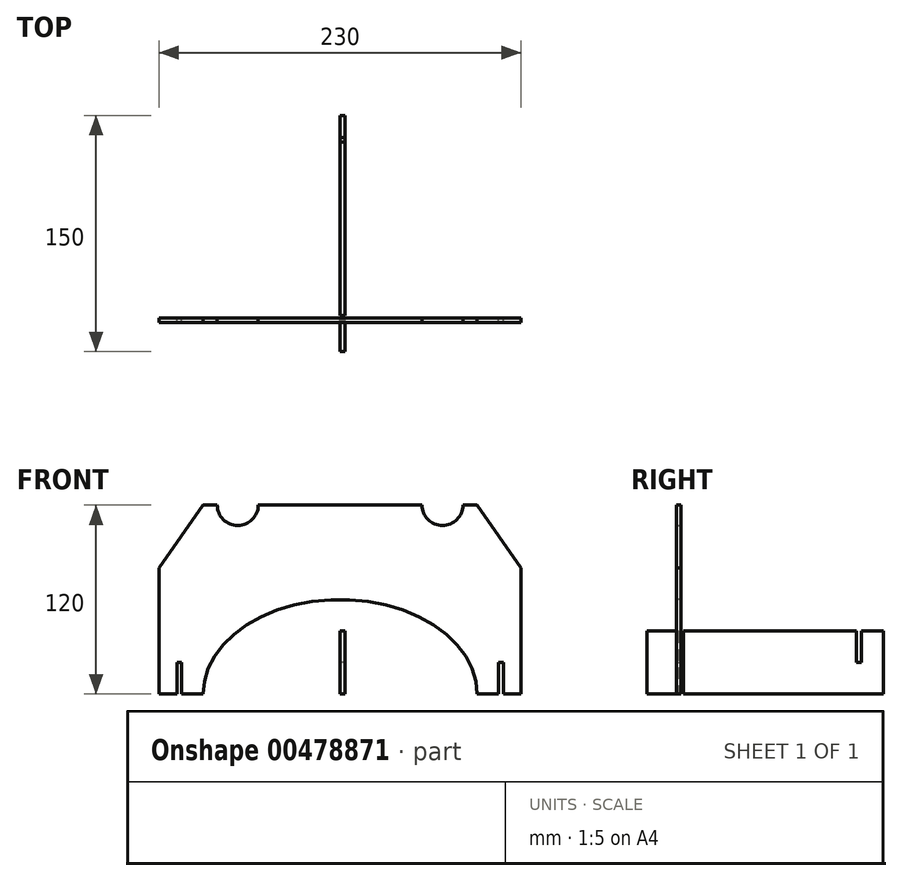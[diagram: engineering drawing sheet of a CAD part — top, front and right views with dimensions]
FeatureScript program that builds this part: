
annotation { "Feature Type Name" : "Feature", "Feature Type Description" : "" }
export const myFeature = defineFeature(function(context is Context, id is Id, definition is map)
    precondition{}
    {
        {
            var Q0;
            Q0=qCreatedBy(makeId("Front.planeOp"),FACE);
            var sketch = newSketch(context, id + "F0", { "sketchPlane" : qUnion([Q0])});
            skLineSegment(sketch, "E0.bottom", {"start": v(-65, 60) * mm, "end": v(65, 60) * mm, "construction": true});
            skLineSegment(sketch, "E0.top", {"start": v(-65, -60) * mm, "end": v(65, -60) * mm, "construction": true});
            skLineSegment(sketch, "E0.left", {"start": v(-65, 60) * mm, "end": v(-65, -60) * mm, "construction": true});
            skLineSegment(sketch, "E0.right", {"start": v(65, 60) * mm, "end": v(65, -60) * mm, "construction": true});
            skPoint(sketch, "E0.middle", {"position": v(0, 0) * mm});
            skLineSegment(sketch, "E1.bottom", {"start": v(65, -60) * mm, "end": v(115, -60) * mm, "construction": true});
            skLineSegment(sketch, "E1.top", {"start": v(65, 60) * mm, "end": v(115, 60) * mm, "construction": true});
            skLineSegment(sketch, "E1.left", {"start": v(65, -60) * mm, "end": v(65, 60) * mm, "construction": true});
            skLineSegment(sketch, "E1.right", {"start": v(115, -60) * mm, "end": v(115, 60) * mm, "construction": true});
            skLineSegment(sketch, "E2.bottom", {"start": v(-65, -60) * mm, "end": v(-115, -60) * mm, "construction": true});
            skLineSegment(sketch, "E2.top", {"start": v(-65, 60) * mm, "end": v(-115, 60) * mm, "construction": true});
            skLineSegment(sketch, "E2.left", {"start": v(-65, -60) * mm, "end": v(-65, 60) * mm, "construction": true});
            skLineSegment(sketch, "E2.right", {"start": v(-115, -60) * mm, "end": v(-115, 60) * mm, "construction": true});
            skCircle(sketch, "E3", {"center": v(65, 60) * mm, "radius": 13 * mm});
            skCircle(sketch, "E4", {"center": v(-65, 60) * mm, "radius": 13 * mm});
            skLineSegment(sketch, "E5", {"start": v(87, 60) * mm, "end": v(115, 20) * mm, "construction": true});
            skLineSegment(sketch, "E6", {"start": v(115, 20) * mm, "end": v(-115, 20) * mm, "construction": true});
            skLineSegment(sketch, "E7", {"start": v(-115, 20) * mm, "end": v(-87, 60) * mm, "construction": true});
            skLineSegment(sketch, "E8", {"start": v(-115, 20) * mm, "end": v(-87, 60) * mm});
            skLineSegment(sketch, "E9", {"start": v(-115, 20) * mm, "end": v(-115, -60) * mm});
            skLineSegment(sketch, "E10", {"start": v(115, -60) * mm, "end": v(-115, -60) * mm});
            skLineSegment(sketch, "E11", {"start": v(115, -60) * mm, "end": v(115, 20) * mm});
            skLineSegment(sketch, "E12", {"start": v(115, 20) * mm, "end": v(87, 60) * mm});
            skPoint(sketch, "E13", {"position": v(52, 60) * mm});
            skPoint(sketch, "E14", {"position": v(78, 60) * mm});
            skPoint(sketch, "E15", {"position": v(-52, 60) * mm});
            skPoint(sketch, "E16", {"position": v(-78, 60) * mm});
            skLineSegment(sketch, "E17", {"start": v(-87, 60) * mm, "end": v(-78, 60) * mm});
            skLineSegment(sketch, "E18", {"start": v(-52, 60) * mm, "end": v(52, 60) * mm});
            skLineSegment(sketch, "E19", {"start": v(78, 60) * mm, "end": v(87, 60) * mm});
            skLineSegment(sketch, "E20", {"start": v(87, 60) * mm, "end": v(87, -67.3) * mm, "construction": true});
            skPoint(sketch, "E21", {"position": v(87, -60) * mm});
            skLineSegment(sketch, "E22.bottom", {"start": v(-103.62, -60) * mm, "end": v(-100.62, -60) * mm});
            skLineSegment(sketch, "E22.top", {"start": v(-103.62, -40) * mm, "end": v(-100.62, -40) * mm});
            skLineSegment(sketch, "E22.left", {"start": v(-103.62, -60) * mm, "end": v(-103.62, -40) * mm});
            skLineSegment(sketch, "E22.right", {"start": v(-100.62, -60) * mm, "end": v(-100.62, -40) * mm});
            skLineSegment(sketch, "E23.MirrorCS", {"start": v(100.62, -60) * mm, "end": v(100.62, -40) * mm});
            skLineSegment(sketch, "E24.MirrorCS", {"start": v(103.62, -60) * mm, "end": v(103.62, -40) * mm});
            skLineSegment(sketch, "E25.MirrorCS", {"start": v(103.62, -40) * mm, "end": v(100.62, -40) * mm});
            skEllipse(sketch, "E26", {"center": v(0, -60) * mm, "majorRadius": 87 * mm, "minorRadius": 60 * mm, "majorAxis": v(1, 0)});
            skFitSpline(sketch, "E27.0", {"points": [v(101.9, -64.06) * mm, v(102.05, -60) * mm, v(101.9, -55.94) * mm, v(101.32, -50.58) * mm, v(99.9, -44.01) * mm, v(97.13, -36.44) * mm, v(93.39, -29.24) * mm, v(88.75, -22.49) * mm, v(84.2, -17.25) * mm, v(80.18, -13.3) * mm, v(76.99, -10.48) * mm, v(74.17, -8.23) * mm, v(71.84, -6.49) * mm, v(70.04, -5.22) * mm, v(68.2, -3.99) * mm, v(65.72, -2.4) * mm, v(62.54, -0.5) * mm, v(58.6, 1.61) * mm, v(53.2, 4.23) * mm, v(46.2, 7.11) * mm, v(37.46, 9.96) * mm, v(28.42, 12.2) * mm, v(20.68, 13.53) * mm, v(14.4, 14.3) * mm, v(9.63, 14.7) * mm, v(5.63, 14.9) * mm, v(2.42, 14.99) * mm, v(0, 15) * mm, v(-2.42, 14.99) * mm, v(-5.63, 14.9) * mm, v(-9.63, 14.7) * mm, v(-14.4, 14.3) * mm, v(-20.68, 13.53) * mm, v(-28.42, 12.2) * mm, v(-37.46, 9.96) * mm, v(-46.2, 7.11) * mm, v(-53.2, 4.23) * mm, v(-58.6, 1.61) * mm, v(-62.54, -0.5) * mm, v(-65.72, -2.4) * mm, v(-68.2, -3.99) * mm, v(-70.04, -5.22) * mm, v(-71.84, -6.49) * mm, v(-74.17, -8.23) * mm, v(-76.99, -10.48) * mm, v(-80.18, -13.3) * mm, v(-84.2, -17.25) * mm, v(-88.75, -22.49) * mm, v(-93.39, -29.24) * mm, v(-97.13, -36.44) * mm, v(-99.9, -44.01) * mm, v(-101.32, -50.58) * mm, v(-101.9, -55.94) * mm, v(-102.05, -60) * mm, v(-101.9, -64.06) * mm, v(-101.32, -69.42) * mm, v(-99.9, -75.99) * mm, v(-97.13, -83.56) * mm, v(-93.39, -90.76) * mm, v(-88.75, -97.51) * mm, v(-84.2, -102.75) * mm, v(-80.18, -106.7) * mm, v(-76.99, -109.52) * mm, v(-74.17, -111.77) * mm, v(-71.84, -113.51) * mm, v(-70.04, -114.78) * mm, v(-68.2, -116.01) * mm, v(-65.72, -117.6) * mm, v(-62.54, -119.5) * mm, v(-58.6, -121.61) * mm, v(-53.2, -124.23) * mm, v(-46.2, -127.11) * mm, v(-37.46, -129.96) * mm, v(-28.42, -132.2) * mm, v(-20.68, -133.53) * mm, v(-14.4, -134.3) * mm, v(-9.63, -134.7) * mm, v(-5.63, -134.9) * mm, v(-2.42, -134.99) * mm, v(0, -135) * mm, v(2.42, -134.99) * mm, v(5.63, -134.9) * mm, v(9.63, -134.7) * mm, v(14.4, -134.3) * mm, v(20.68, -133.53) * mm, v(28.42, -132.2) * mm, v(37.46, -129.96) * mm, v(46.2, -127.11) * mm, v(53.2, -124.23) * mm, v(58.6, -121.61) * mm, v(62.54, -119.5) * mm, v(65.72, -117.6) * mm, v(68.2, -116.01) * mm, v(70.04, -114.78) * mm, v(71.84, -113.51) * mm, v(74.17, -111.77) * mm, v(76.99, -109.52) * mm, v(80.18, -106.7) * mm, v(84.2, -102.75) * mm, v(88.75, -97.51) * mm, v(93.39, -90.76) * mm, v(97.13, -83.56) * mm, v(99.9, -75.99) * mm, v(101.32, -69.42) * mm, v(101.9, -64.06) * mm, v(102.05, -60) * mm, v(101.9, -55.94) * mm, v(101.9, -64.06) * mm], "construction": true});
            skPoint(sketch, "E28", {"position": v(102, -60) * mm});
            skPoint(sketch, "E29", {"position": v(-102, -60) * mm});
            skSolve(sketch);
        }
        {
            var Q0;
            Q0=makeQuery(id+"F0.imprint","IMPRINT",FACE,{"disambiguationData":[TD([[makeQuery(id+"F0.imprint","IMPRINT",EDGE,{"derivedFrom":sQuery(id+"F0.wireOp",EDGE,"E8")}),-1.0]])]});
            extrude(context, id + "F1", {"entities" : qUnion([Q0]), "depth" : 3 * mm});
        }
        {
            var Q0;
            Q0=qCreatedBy(makeId("Right.planeOp"),FACE);
            var sketch = newSketch(context, id + "F2", { "sketchPlane" : qUnion([Q0])});
            skLineSegment(sketch, "E30.bottom", {"start": v(-21.5, -60) * mm, "end": v(128.5, -60) * mm});
            skLineSegment(sketch, "E30.top", {"start": v(-21.5, -20) * mm, "end": v(128.5, -20) * mm});
            skLineSegment(sketch, "E30.left", {"start": v(-21.5, -60) * mm, "end": v(-21.5, -20) * mm});
            skLineSegment(sketch, "E30.right", {"start": v(128.5, -60) * mm, "end": v(128.5, -20) * mm});
            skPoint(sketch, "E31.0", {"position": v(0, -40) * mm});
            skLineSegment(sketch, "E32.bottom", {"start": v(-1.5, -20) * mm, "end": v(1.5, -20) * mm});
            skLineSegment(sketch, "E32.top", {"start": v(-1.5, -60) * mm, "end": v(1.5, -60) * mm});
            skLineSegment(sketch, "E32.left", {"start": v(-1.5, -20) * mm, "end": v(-1.5, -60) * mm});
            skLineSegment(sketch, "E32.right", {"start": v(1.5, -20) * mm, "end": v(1.5, -60) * mm});
            skLineSegment(sketch, "E33", {"start": v(0, -40) * mm, "end": v(1.5, -40) * mm});
            skLineSegment(sketch, "E34", {"start": v(0, -40) * mm, "end": v(-1.5, -40) * mm});
            skLineSegment(sketch, "E35", {"start": v(1.5, -20) * mm, "end": v(111.5, -20) * mm, "construction": true});
            skLineSegment(sketch, "E36", {"start": v(56.5, -20) * mm, "end": v(56.5, -66.14) * mm, "construction": true});
            skLineSegment(sketch, "E37.MirrorCS", {"start": v(114.5, -20) * mm, "end": v(114.5, -60) * mm});
            skLineSegment(sketch, "E38.MirrorCS", {"start": v(111.5, -20) * mm, "end": v(111.5, -60) * mm});
            skLineSegment(sketch, "E39.MirrorCS", {"start": v(113, -40) * mm, "end": v(114.5, -40) * mm});
            skLineSegment(sketch, "E40.MirrorCS", {"start": v(113, -40) * mm, "end": v(111.5, -40) * mm});
            skSolve(sketch);
        }
        {
            var Q0;
            {var subQ1=sQuery(id+"F2.wireOp",EDGE,"E30.top");var subQ6=sQuery(id+"F2.wireOp",EDGE,"E38.MirrorCS");var subQ7=makeQuery(id+"F2.imprint","INTERSECT",VERTEX,{"derivedFrom":[subQ1,subQ6]});Q0=makeQuery(id+"F2.imprint","IMPRINT",FACE,{"disambiguationData":[TD([[makeQuery(id+"F2.imprint","IMPRINT",EDGE,{"disambiguationData":[TD([[subQ7,-1.0]])],"derivedFrom":subQ6}),-1.0]])]});}
            var Q1;
            {var subQ4=sQuery(id+"F2.wireOp",EDGE,"E30.left");Q1=makeQuery(id+"F2.imprint","IMPRINT",FACE,{"disambiguationData":[TD([[makeQuery(id+"F2.imprint","IMPRINT",EDGE,{"derivedFrom":subQ4}),-1.0]])]});}
            var Q2;
            {var subQ1=sQuery(id+"F2.wireOp",EDGE,"E32.top");Q2=makeQuery(id+"F2.imprint","IMPRINT",FACE,{"disambiguationData":[TD([[makeQuery(id+"F2.imprint","IMPRINT",EDGE,{"derivedFrom":subQ1}),1.0]])]});}
            var Q3;
            {var subQ6=sQuery(id+"F2.wireOp",EDGE,"E39.MirrorCS");Q3=makeQuery(id+"F2.imprint","IMPRINT",FACE,{"disambiguationData":[TD([[makeQuery(id+"F2.imprint","IMPRINT",EDGE,{"derivedFrom":subQ6}),-1.0]])]});}
            var Q4;
            {var subQ0=sQuery(id+"F2.wireOp",EDGE,"E30.right");Q4=makeQuery(id+"F2.imprint","IMPRINT",FACE,{"disambiguationData":[TD([[makeQuery(id+"F2.imprint","IMPRINT",EDGE,{"derivedFrom":subQ0}),1.0]])]});}
            extrude(context, id + "F3", {"entities" : qUnion([Q0, Q1, Q2, Q3, Q4]), "depth" : 3 * mm});
        }
    });
